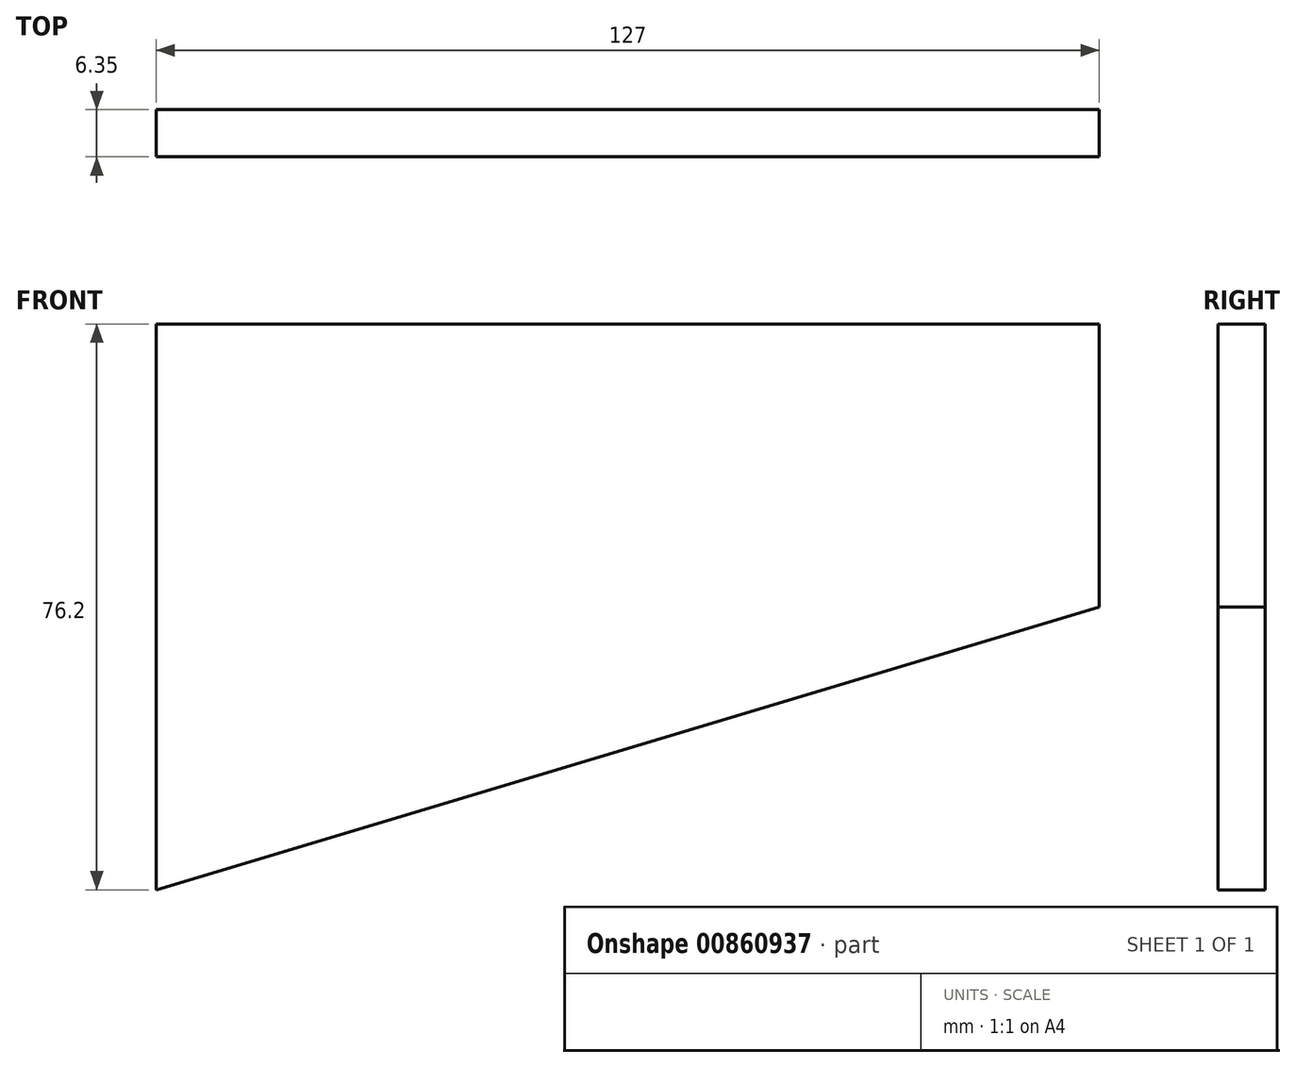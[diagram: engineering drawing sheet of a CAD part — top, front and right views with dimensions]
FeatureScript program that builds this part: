
annotation { "Feature Type Name" : "Feature", "Feature Type Description" : "" }
export const myFeature = defineFeature(function(context is Context, id is Id, definition is map)
    precondition{}
    {
        {
            var Q0;
            Q0=qCreatedBy(makeId("Front.planeOp"),FACE);
            var sketch = newSketch(context, id + "F0", { "sketchPlane" : qUnion([Q0])});
            skLineSegment(sketch, "E0", {"start": v(-77.34, 52.82) * mm, "end": v(49.66, 52.82) * mm});
            skLineSegment(sketch, "E1", {"start": v(49.66, 52.82) * mm, "end": v(49.66, 14.72) * mm});
            skLineSegment(sketch, "E2", {"start": v(49.66, 14.72) * mm, "end": v(-77.34, -23.38) * mm});
            skLineSegment(sketch, "E3", {"start": v(-77.34, -23.38) * mm, "end": v(-77.34, 52.82) * mm});
            skSolve(sketch);
        }
        {
            var Q0;
            Q0 = qSketchRegion(id + "F0", true);
            extrude(context, id + "F1", {"entities" : qUnion([Q0]), "depth" : 6.35 * mm, "offsetDistance" : 25.4 * mm});
        }
    });
